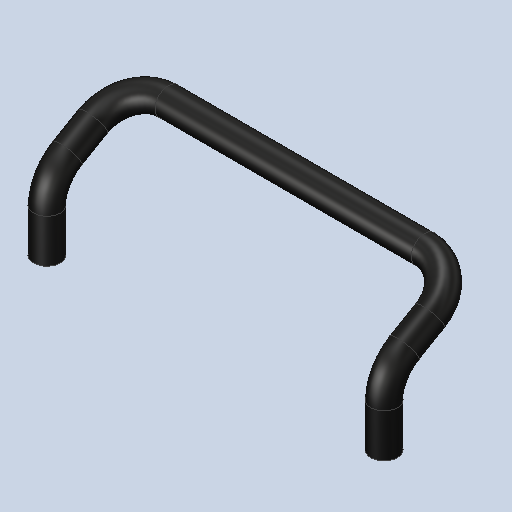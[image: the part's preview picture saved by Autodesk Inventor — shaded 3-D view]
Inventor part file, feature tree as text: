
AUTODESK INVENTOR PART (.ipt)
format: ipt  version: 2024.2 (Build 282272000, 272)  size: 345,600 bytes
history: native  units: mm
features: other x14, extrude x5, revolve x4, hole x2, sketch x2
ambient origin geometry x8: Origin, YZ Plane, XZ Plane, XY Plane, X Axis, Y Axis, Z Axis, Center Point
bodies: Solid1 (feature_tree)
feature tree (27):
  extrude  "Extrusion1"  TaperAngle=60.0deg  [1 undecoded]
  revolve  "Revolution1"  Angle=90.0deg
  extrude  "Extrusion2"  Depth=5.0mm TaperAngle=0.0deg
  revolve  "Revolution2"  Angle=90.0deg
  extrude  "Extrusion3"  Depth=5.0mm TaperAngle=0.0deg
  revolve  "Revolution3"  Angle=60.0deg
  extrude  "Extrusion4"  Depth=5.0mm TaperAngle=0.0deg
  revolve  "Revolution4"  [1 undecoded]
  extrude  "Extrusion5"  [1 undecoded]
  hole  "Hole1"  [1 undecoded]
  hole  "Hole2"  [1 undecoded]
  other  "H1_XY"
  other  "H1_YZ"
  other  "H1_ZX"
  other  "H1_X"
  other  "H1_Y"
  other  "H1_Z"
  other  "H1_Center"
  other  "H2_XY"
  other  "H2_YZ"
  other  "H2_ZX"
  other  "H2_X"
  other  "H2_Y"
  other  "H2_Z"
  other  "H2_Center"
  sketch  "Sketch10"  dims[d0=16.01924mm d1=0.0mm d2=60.0deg]
  sketch  "Sketch11"  dims[d3=10.98076mm d4=0.0mm d5=90.0deg d6=95.0mm d7=0.0mm d8=90.0deg d9=10.98076mm d10=0.0mm d11=60.0deg d12=16.01924mm d13=0.0mm d14=4.134mm d15=13.0mm d16=5.0mm d17=2.0mm d18=90.0deg d19=15.6mm d20=120.0deg d21=4.134mm d22=13.0mm d23=5.0mm d24=2.0mm d25=90.0deg d26=15.6mm d27=120.0deg d28=0.0mm d29=0.0mm]
note: 5 required parameter values undecoded (feature->parameter linkage not recoverable at this tier; creation-order binding heuristic only, values carry confidence <= 0.55)